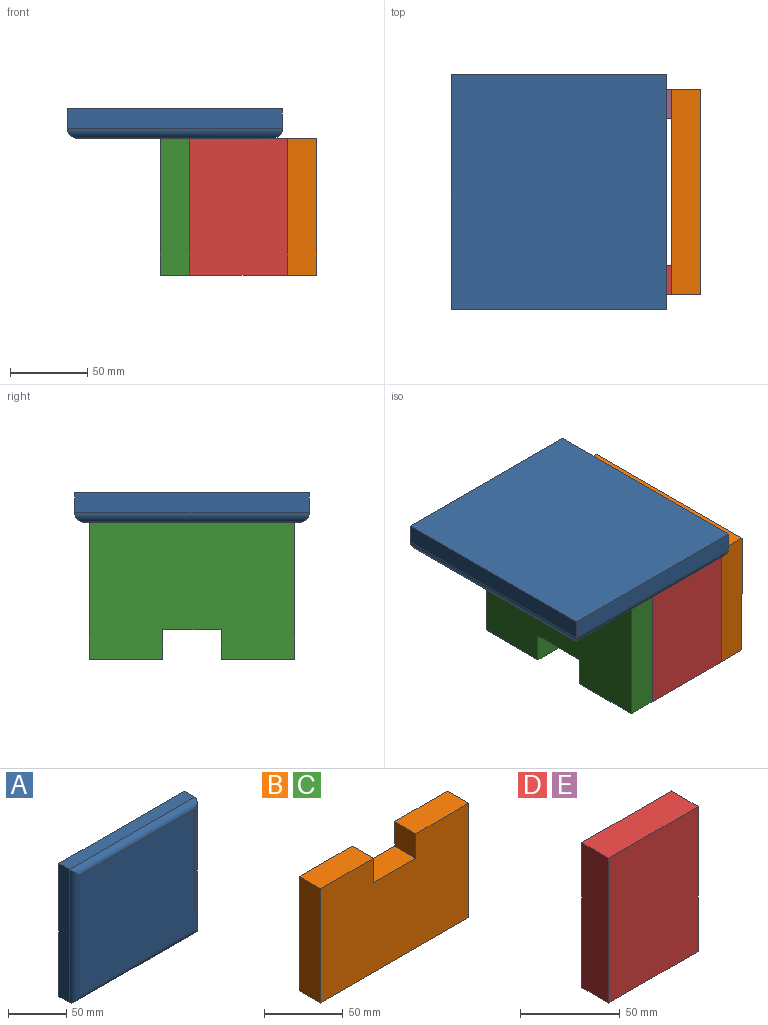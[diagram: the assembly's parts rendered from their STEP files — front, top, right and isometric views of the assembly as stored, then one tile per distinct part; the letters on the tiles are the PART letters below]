
ASSEMBLY  parts=5 mates=11
PART A: 10 faces, bbox 152.4x19.1x139.7 mm
  f0: plane 139.7x12.7mm, normal (-1,0,0), area 1774.2mm2, adj f1,f3,f5,f6
  f1: plane 152.4x12.7mm, normal (0,0,-1), area 1935.5mm2, adj f0,f2,f5,f7
  f2: plane 139.7x12.7mm, normal (1,0,0), area 1774.2mm2, adj f1,f3,f5,f9
  f3: plane 152.4x12.7mm, normal (0,0,1), area 1935.5mm2, adj f0,f2,f5,f8
  f4: plane 139.7x127mm, normal (0,-1,0), area 17741.9mm2, adj f6,f7,f8,f9
  f5: plane 152.4x139.7mm, normal (0,1,0), area 21290.3mm2, adj f0,f1,f2,f3
  f6: cylinder r=6.35mm len=139.7mm, axis (0,0,1), area 1347.4mm2, adj f0,f4,f7,f8
  f7: cylinder r=6.35mm len=152.4mm, axis (-1,0,0), area 1474.1mm2, adj f1,f4,f6,f9
  f8: cylinder r=6.35mm len=152.4mm, axis (1,0,0), area 1474.1mm2, adj f3,f4,f6,f9
  f9: cylinder r=6.35mm len=139.7mm, axis (0,0,-1), area 1347.4mm2, adj f2,f4,f7,f8
PART B: 10 faces, bbox 133.4x19.1x88.9 mm
  f0: plane 47.63x19.05mm, normal (0,0,1), area 907.3mm2, adj f1,f7,f8,f9
  f1: plane 88.9x19.05mm, normal (-1,0,0), area 1693.5mm2, adj f0,f2,f8,f9
  f2: plane 133.35x19.05mm, normal (0,0,-1), area 2540.3mm2, adj f1,f3,f8,f9
  f3: plane 88.9x19.05mm, normal (1,0,0), area 1693.5mm2, adj f2,f4,f8,f9
  f4: plane 47.63x19.05mm, normal (0,0,1), area 907.3mm2, adj f3,f5,f8,f9
  f5: plane 19.05x19.05mm, normal (-1,0,0), area 362.9mm2, adj f4,f6,f8,f9
  f6: plane 38.1x19.05mm, normal (0,0,1), area 725.8mm2, adj f5,f7,f8,f9
  f7: plane 19.05x19.05mm, normal (1,0,0), area 362.9mm2, adj f0,f6,f8,f9
  f8: plane 133.35x88.9mm, normal (0,-1,0), area 11129mm2, adj f0,f1,f2,f3,f4,f5,f6,f7
  f9: plane 133.35x88.9mm, normal (0,1,0), area 11129mm2, adj f0,f1,f2,f3,f4,f5,f6,f7
PART C: same geometry as B
PART D: 6 faces, bbox 63.5x19.1x88.9 mm
  f0: plane 88.9x19.05mm, normal (-1,0,0), area 1693.5mm2, adj f1,f3,f4,f5
  f1: plane 63.5x19.05mm, normal (0,0,-1), area 1209.7mm2, adj f0,f2,f4,f5
  f2: plane 88.9x19.05mm, normal (1,0,0), area 1693.5mm2, adj f1,f3,f4,f5
  f3: plane 63.5x19.05mm, normal (0,0,1), area 1209.7mm2, adj f0,f2,f4,f5
  f4: plane 88.9x63.5mm, normal (0,-1,0), area 5645.2mm2, adj f0,f1,f2,f3
  f5: plane 88.9x63.5mm, normal (0,1,0), area 5645.2mm2, adj f0,f1,f2,f3
PART E: same geometry as D
PLACE A rot(axis=(0.58,-0.58,-0.58),120deg) t=(-32.72,-91.99,184.66)mm
PLACE B rot(axis=(-0.71,-0.71,0),180deg) t=(61.22,-76.2,103.99)mm
PLACE C rot(axis=(-0.71,-0.71,0),180deg) t=(-21.33,-76.2,103.99)mm
PLACE D rot(axis=(0,-1,0),180deg) t=(-1.39,-142.88,122.16)mm
PLACE E t=(22.23,-28.58,120.17)mm
MATE planar E.f3 <-> B.f2  axis (0,0,1) through (10.42,-38.1,165.61)mm
MATE parallel C.f8 <-> B.f8  axis (-1,0,0) through (-40.38,-95.25,123.44)mm
MATE planar D.f3 <-> C.f0  axis (0,0,-1) through (10.42,-152.4,76.71)mm
MATE planar D.f2 <-> C.f9  axis (-1,0,0) through (-21.33,-152.4,121.16)mm
MATE planar C.f3 <-> E.f5  axis (0,1,0) through (-30.86,-28.58,121.16)mm
MATE planar C.f1 <-> D.f4  axis (0,-1,0) through (-30.86,-161.93,121.16)mm
MATE planar A.f4 <-> C.f2  axis (0,0,-1) through (-30.86,-95.25,165.61)mm
MATE planar E.f1 <-> C.f4  axis (0,0,-1) through (10.42,-38.1,76.71)mm
MATE planar E.f5 <-> B.f3  axis (0,1,0) through (10.42,-28.58,121.16)mm
MATE planar B.f8 <-> D.f0  axis (-1,0,0) through (42.17,-95.25,123.44)mm
MATE planar C.f9 <-> E.f0  axis (1,0,0) through (-21.33,-95.25,123.44)mm
